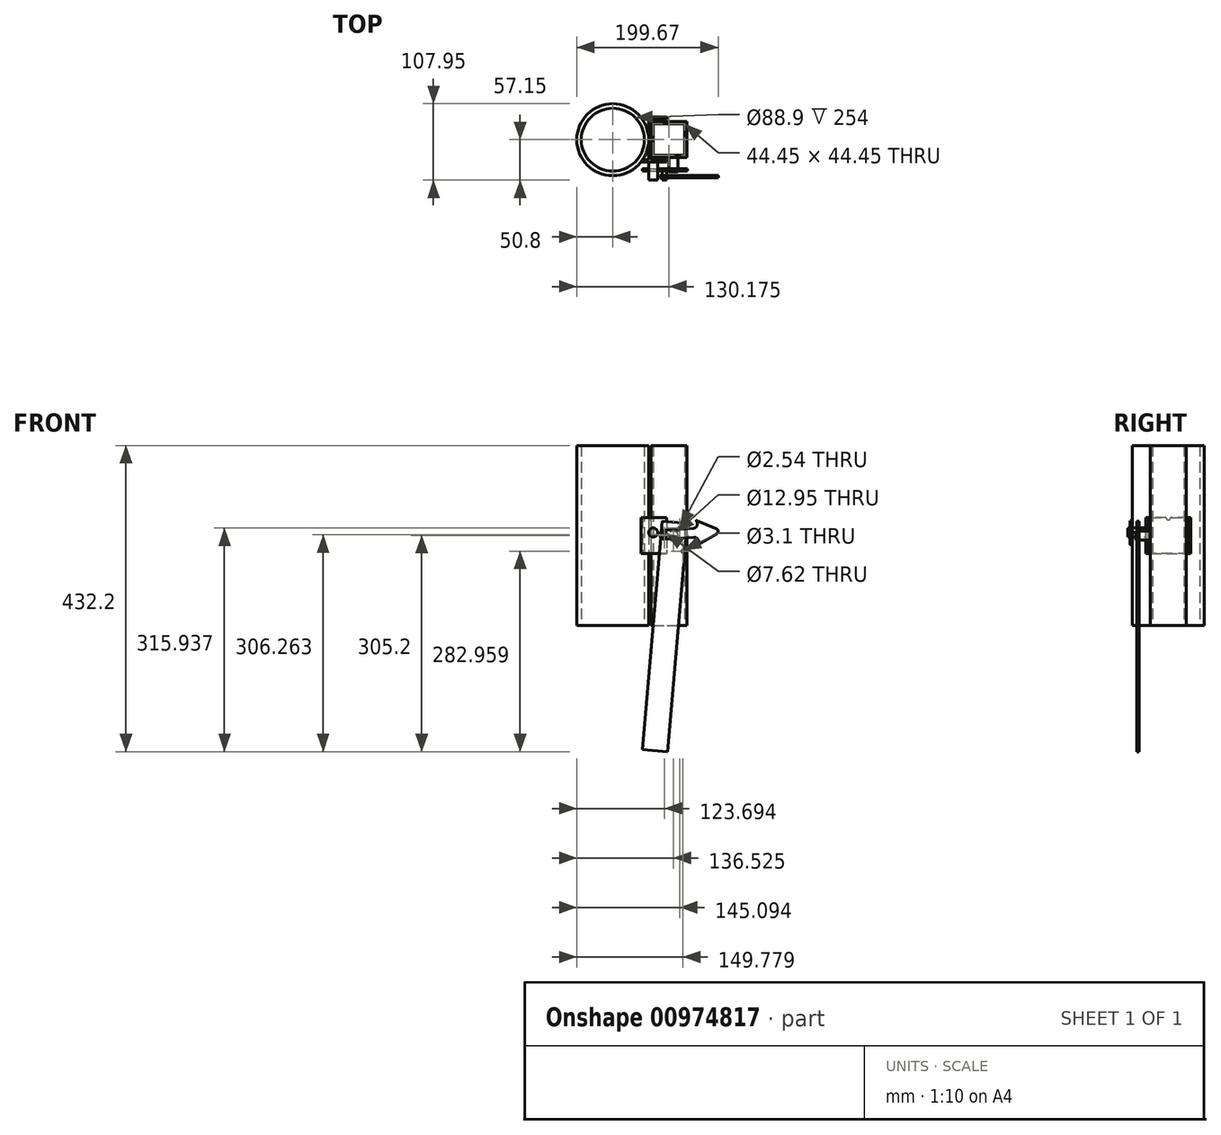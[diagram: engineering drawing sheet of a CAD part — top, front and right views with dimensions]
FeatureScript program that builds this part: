
annotation { "Feature Type Name" : "Feature", "Feature Type Description" : "" }
export const myFeature = defineFeature(function(context is Context, id is Id, definition is map)
    precondition{}
    {
        {
            var Q0;
            Q0=qCreatedBy(makeId("Top.planeOp"),FACE);
            var sketch = newSketch(context, id + "F0", { "sketchPlane" : qUnion([Q0])});
            skLineSegment(sketch, "E0", {"start": v(25.4, 31.75) * mm, "end": v(0, 31.75) * mm});
            skLineSegment(sketch, "E1", {"start": v(0, 31.75) * mm, "end": v(0, -31.75) * mm});
            skLineSegment(sketch, "E2", {"start": v(0, -31.75) * mm, "end": v(25.4, -31.75) * mm});
            skLineSegment(sketch, "E3", {"start": v(25.4, -31.75) * mm, "end": v(25.4, -28.57) * mm});
            skLineSegment(sketch, "E4", {"start": v(25.4, -28.57) * mm, "end": v(3.17, -28.57) * mm});
            skLineSegment(sketch, "E5", {"start": v(3.17, -28.57) * mm, "end": v(3.17, 28.57) * mm});
            skLineSegment(sketch, "E6", {"start": v(3.17, 28.57) * mm, "end": v(25.4, 28.57) * mm});
            skLineSegment(sketch, "E7", {"start": v(25.4, 28.57) * mm, "end": v(25.4, 31.75) * mm});
            skCircle(sketch, "E8", {"center": v(-50.8, 0) * mm, "radius": 50.8 * mm, "construction": true});
            skLineSegment(sketch, "E9", {"start": v(0, 28.57) * mm, "end": v(-8.8, 28.57) * mm});
            skLineSegment(sketch, "E10", {"start": v(0, 31.75) * mm, "end": v(-11.14, 31.75) * mm});
            skLineSegment(sketch, "E11", {"start": v(0, -28.57) * mm, "end": v(-8.8, -28.57) * mm});
            skLineSegment(sketch, "E12", {"start": v(0, -31.75) * mm, "end": v(-11.14, -31.75) * mm});
            skArc(sketch, "E13", {"start": v(-8.8, 28.57) * mm, "mid": v(-9.94, 30.19) * mm, "end": v(-11.14, 31.75) * mm});
            skArc(sketch, "E14", {"start": v(-11.14, -31.75) * mm, "mid": v(-9.94, -30.19) * mm, "end": v(-8.8, -28.57) * mm});
            skLineSegment(sketch, "E15", {"start": v(-100.23, -63.5) * mm, "end": v(128.61, -63.5) * mm, "construction": true});
            skLineSegment(sketch, "E16", {"start": v(-100.58, -69.85) * mm, "end": v(131.7, -69.85) * mm, "construction": true});
            skLineSegment(sketch, "E17", {"start": v(0, 0) * mm, "end": v(0, -25.4) * mm, "construction": true});
            skLineSegment(sketch, "E18", {"start": v(0, -25.4) * mm, "end": v(-6.8, -25.4) * mm, "construction": true});
            skSolve(sketch);
        }
        {
            var Q0;
            {var subQ2=sQuery(id+"F0.wireOp",EDGE,"E9");Q0=makeQuery(id+"F0.imprint","IMPRINT",FACE,{"disambiguationData":[TD([[makeQuery(id+"F0.imprint","IMPRINT",EDGE,{"derivedFrom":subQ2}),-1.0]])]});}
            var Q1;
            {var subQ3=sQuery(id+"F0.wireOp",EDGE,"E0");Q1=makeQuery(id+"F0.imprint","IMPRINT",FACE,{"disambiguationData":[TD([[makeQuery(id+"F0.imprint","IMPRINT",EDGE,{"derivedFrom":subQ3}),1.0]])]});}
            var Q2;
            {var subQ2=sQuery(id+"F0.wireOp",EDGE,"E11");Q2=makeQuery(id+"F0.imprint","IMPRINT",FACE,{"disambiguationData":[TD([[makeQuery(id+"F0.imprint","IMPRINT",EDGE,{"derivedFrom":subQ2}),1.0]])]});}
            extrude(context, id + "F1", {"entities" : qUnion([Q0, Q1, Q2]), "endBound" : BoundingType.SYMMETRIC, "depth" : 50.8 * mm, "offsetDistance" : 25.4 * mm});
        }
        {
            var Q0;
            Q0=makeQuery(id+"F1.opExtrude","SWEPT_FACE",FACE,{"disambiguationData":[OSD([sQuery(id+"F0.wireOp",EDGE,"E5")])]});
            var sketch = newSketch(context, id + "F2", { "sketchPlane" : qUnion([Q0])});
            skCircle(sketch, "E19", {"center": v(0, 25.4) * mm, "radius": 3.18 * mm});
            skSolve(sketch);
        }
        {
            var Q0;
            Q0=qSketchRegion(id+"F2",true);
            extrude(context, id + "F3", {"entities" : qUnion([Q0]), "operationType" : NewBodyOperationType.REMOVE, "endBound" : BoundingType.THROUGH_ALL, "oppositeDirection" : true, "depth" : 25.4 * mm, "offsetDistance" : 25.4 * mm});
        }
        {
            var Q0;
            Q0=qCreatedBy(makeId("Top.planeOp"),FACE);
            var sketch = newSketch(context, id + "F4", { "sketchPlane" : qUnion([Q0])});
            skCircle(sketch, "E20", {"center": v(-50.8, 0) * mm, "radius": 50.8 * mm});
            skCircle(sketch, "E21", {"center": v(-50.8, 0) * mm, "radius": 44.45 * mm});
            skLineSegment(sketch, "E22.bottom", {"start": v(3.17, 25.4) * mm, "end": v(53.97, 25.4) * mm});
            skLineSegment(sketch, "E22.top", {"start": v(3.18, -25.4) * mm, "end": v(53.98, -25.4) * mm});
            skLineSegment(sketch, "E22.left", {"start": v(3.17, 25.4) * mm, "end": v(3.18, -25.4) * mm});
            skLineSegment(sketch, "E22.right", {"start": v(53.97, 25.4) * mm, "end": v(53.98, -25.4) * mm});
            skLineSegment(sketch, "E23.bottom", {"start": v(6.35, 22.22) * mm, "end": v(50.8, 22.23) * mm});
            skLineSegment(sketch, "E23.top", {"start": v(6.35, -22.23) * mm, "end": v(50.8, -22.22) * mm});
            skLineSegment(sketch, "E23.left", {"start": v(6.35, 22.22) * mm, "end": v(6.35, -22.23) * mm});
            skLineSegment(sketch, "E23.right", {"start": v(50.8, 22.23) * mm, "end": v(50.8, -22.22) * mm});
            skSolve(sketch);
        }
        {
            var Q0;
            Q0=qSketchRegion(id+"F4",true);
            extrude(context, id + "F5", {"entities" : qUnion([Q0]), "endBound" : BoundingType.SYMMETRIC, "depth" : 254 * mm, "offsetDistance" : 25.4 * mm});
        }
        {
            var Q0;
            Q0=makeQuery(id+"F1.opExtrude","SWEPT_FACE",FACE,{"disambiguationData":[OSD([sQuery(id+"F0.wireOp",EDGE,"E2"),sQuery(id+"F0.wireOp",EDGE,"E12")])]});
            var sketch = newSketch(context, id + "F6", { "sketchPlane" : qUnion([Q0])});
            skCircle(sketch, "E24", {"center": v(6.24, 4.27) * mm, "radius": 6.35 * mm});
            skSolve(sketch);
        }
        {
            var Q0;
            Q0=qSketchRegion(id+"F6",true);
            extrude(context, id + "F7", {"entities" : qUnion([Q0]), "operationType" : NewBodyOperationType.ADD, "depth" : 25.4 * mm, "offsetDistance" : 25.4 * mm});
        }
        {
            var Q0;
            Q0=makeQuery(id+"F5.opExtrude","SWEPT_FACE",FACE,{"disambiguationData":[OSD([sQuery(id+"F4.wireOp",EDGE,"E22.top")])]});
            var sketch = newSketch(context, id + "F8", { "sketchPlane" : qUnion([Q0])});
            skCircle(sketch, "E25", {"center": v(34.93, 0) * mm, "radius": 6.35 * mm});
            skCircle(sketch, "E26", {"center": v(34.93, 0) * mm, "radius": 6.48 * mm});
            skLineSegment(sketch, "E27.bottom", {"start": v(-8.83, -302.17) * mm, "end": v(26.6, -305.2) * mm});
            skLineSegment(sketch, "E27.top", {"start": v(43.25, 305.2) * mm, "end": v(78.68, 302.17) * mm, "construction": true});
            skLineSegment(sketch, "E27.left", {"start": v(-8.83, -302.17) * mm, "end": v(43.25, 305.2) * mm});
            skLineSegment(sketch, "E27.right", {"start": v(26.6, -305.2) * mm, "end": v(78.68, 302.17) * mm});
            skLineSegment(sketch, "E28", {"start": v(35.9, -0.08) * mm, "end": v(33.58, 0.12) * mm, "construction": true});
            skCircle(sketch, "E29", {"center": v(22.27, 1.08) * mm, "radius": 3.18 * mm});
            skCircle(sketch, "E30", {"center": v(5.37, -47.47) * mm, "radius": 2.49 * mm, "construction": true});
            skLineSegment(sketch, "E31", {"start": v(18.84, 20.5) * mm, "end": v(54.27, 17.46) * mm});
            skCircle(sketch, "E32", {"center": v(43.5, 10.74) * mm, "radius": 1.27 * mm});
            skCircle(sketch, "E33", {"center": v(48.18, -22.24) * mm, "radius": 1.55 * mm});
            skSolve(sketch);
        }
        {
            var Q0;
            Q0=makeQuery(id+"F8.imprint","IMPRINT",FACE,{"disambiguationData":[TD([[makeQuery(id+"F8.imprint","IMPRINT",EDGE,{"derivedFrom":sQuery(id+"F8.wireOp",EDGE,"E25")}),1.0]])]});
            var Q1;
            Q1=makeQuery(id+"F8.imprint","IMPRINT",FACE,{"disambiguationData":[TD([[makeQuery(id+"F8.imprint","IMPRINT",EDGE,{"derivedFrom":sQuery(id+"F8.wireOp",EDGE,"YTCzxCOa-TUTg-SinB-Mg6B-8yEmz2HBc4Hb.bottom")}),1.0]])]});
            var Q2;
            Q2=makeQuery(id+"F8.imprint","IMPRINT",FACE,{"disambiguationData":[TD([[makeQuery(id+"F8.imprint","IMPRINT",EDGE,{"derivedFrom":sQuery(id+"F8.wireOp",EDGE,"uR8Vylv1-tZYr-DXoJ-TwQZ-MpIGQ8XLBA7z.bottom")}),1.0]])]});
            extrude(context, id + "F9", {"entities" : qUnion([Q0, Q1, Q2]), "operationType" : NewBodyOperationType.ADD, "depth" : 20.32 * mm, "offsetDistance" : 25.4 * mm});
        }
        {
            var Q0;
            Q0=qCreatedBy(makeId("Front.planeOp"),FACE);
            var sketch = newSketch(context, id + "F10", { "sketchPlane" : qUnion([Q0])});
            skCircle(sketch, "E34", {"center": v(22.1, 1.06) * mm, "radius": 3.81 * mm});
            skCircle(sketch, "E35", {"center": v(34.93, 0) * mm, "radius": 6.35 * mm, "construction": true});
            skArc(sketch, "E36", {"start": v(21.65, 7.4) * mm, "mid": v(15.76, 0.62) * mm, "end": v(22.54, -5.27) * mm});
            skLineSegment(sketch, "E37", {"start": v(21.65, 7.4) * mm, "end": v(62.83, 10.27) * mm});
            skArc(sketch, "E38", {"start": v(64.82, 22.47) * mm, "mid": v(58.62, 11.5) * mm, "end": v(67.26, 20.68) * mm, "construction": true});
            skLineSegment(sketch, "E39", {"start": v(95.72, 9.62) * mm, "end": v(67.7, 21.27) * mm});
            skArc(sketch, "E40", {"start": v(62.83, 10.27) * mm, "mid": v(68.23, 14.12) * mm, "end": v(67.26, 20.68) * mm});
            skLineSegment(sketch, "E41", {"start": v(22.1, 1.06) * mm, "end": v(119.58, 7.86) * mm, "construction": true});
            skLineSegment(sketch, "E42.MirrorCS", {"start": v(96.2, 2.82) * mm, "end": v(70.06, -12.62) * mm});
            skArc(sketch, "E43.MirrorCS", {"start": v(63.71, -2.4) * mm, "mid": v(69.6, -5.46) * mm, "end": v(69.54, -12.09) * mm});
            skLineSegment(sketch, "E44.MirrorCS", {"start": v(22.54, -5.27) * mm, "end": v(63.71, -2.4) * mm});
            skLineSegment(sketch, "E45", {"start": v(34.92, 57.7) * mm, "end": v(34.93, -40.23) * mm, "construction": true});
            skArc(sketch, "E46", {"start": v(95.72, 9.62) * mm, "mid": v(98.06, 6.36) * mm, "end": v(96.2, 2.82) * mm});
            skPoint(sketch, "E47.orphan", {"position": v(102.76, 6.7) * mm});
            skArc(sketch, "E48", {"start": v(67.7, 21.27) * mm, "mid": v(67.24, 21.15) * mm, "end": v(67.26, 20.68) * mm});
            skArc(sketch, "E49", {"start": v(69.54, -12.09) * mm, "mid": v(69.6, -12.56) * mm, "end": v(70.06, -12.62) * mm});
            skPoint(sketch, "E50.orphan", {"position": v(67.38, -14.2) * mm});
            skSolve(sketch);
        }
        {
            var Q0;
            Q0=makeQuery(id+"F10.imprint","IMPRINT",FACE,{"disambiguationData":[TD([[makeQuery(id+"F10.imprint","IMPRINT",EDGE,{"derivedFrom":sQuery(id+"F10.wireOp",EDGE,"E39")}),1.0]])]});
            var Q1;
            Q1=makeQuery(id+"F10.imprint","IMPRINT",FACE,{"disambiguationData":[TD([[makeQuery(id+"F10.imprint","IMPRINT",EDGE,{"derivedFrom":sQuery(id+"F10.wireOp",EDGE,"E34")}),-1.0]])]});
            var Q2;
            {var subQ1=sQuery(id+"F10.wireOp",EDGE,"E37");var subQ5=sQuery(id+"F10.wireOp",EDGE,"7acd8ec4-8899-4b79-b3ee-c8cdcc686e7c1.MirrorCS");var subQ6=makeQuery(id+"F10.imprint","INTERSECT",VERTEX,{"derivedFrom":[subQ1,subQ5]});Q2=makeQuery(id+"F10.imprint","IMPRINT",FACE,{"disambiguationData":[TD([[makeQuery(id+"F10.imprint","IMPRINT",EDGE,{"disambiguationData":[TD([[subQ6,1.0]])],"derivedFrom":subQ1}),-1.0]])]});}
            extrude(context, id + "F11", {"entities" : qUnion([Q0, Q1, Q2]), "depth" : 53.97 * mm, "offsetDistance" : 25.4 * mm, "hasSecondDirection" : true, "secondDirectionOppositeDirection" : false, "secondDirectionDepth" : 50.8 * mm});
        }
        {
            var Q0;
            Q0 = qSketchRegion(id + "F8", true);
            var Q1;
            Q1=makeQuery(id+"F8.imprint","IMPRINT",FACE,{"disambiguationData":[TD([[makeQuery(id+"F8.imprint","IMPRINT",EDGE,{"derivedFrom":sQuery(id+"F8.wireOp",EDGE,"E29")}),1.0]])]});
            extrude(context, id + "F12", {"entities" : qUnion([Q0, Q1]), "depth" : 19.05 * mm, "offsetDistance" : 25.4 * mm, "hasSecondDirection" : true, "secondDirectionOppositeDirection" : false, "secondDirectionDepth" : 15.88 * mm});
        }
        {
            var Q0;
            Q0=makeQuery(id+"F8.imprint","IMPRINT",FACE,{"disambiguationData":[TD([[makeQuery(id+"F8.imprint","IMPRINT",EDGE,{"derivedFrom":sQuery(id+"F8.wireOp",EDGE,"E29")}),1.0]])]});
            extrude(context, id + "F13", {"entities" : qUnion([Q0]), "operationType" : NewBodyOperationType.ADD, "depth" : 31.75 * mm, "offsetDistance" : 25.4 * mm, "hasSecondDirection" : true, "secondDirectionOppositeDirection" : false, "secondDirectionDepth" : 19.05 * mm});
        }
    });
